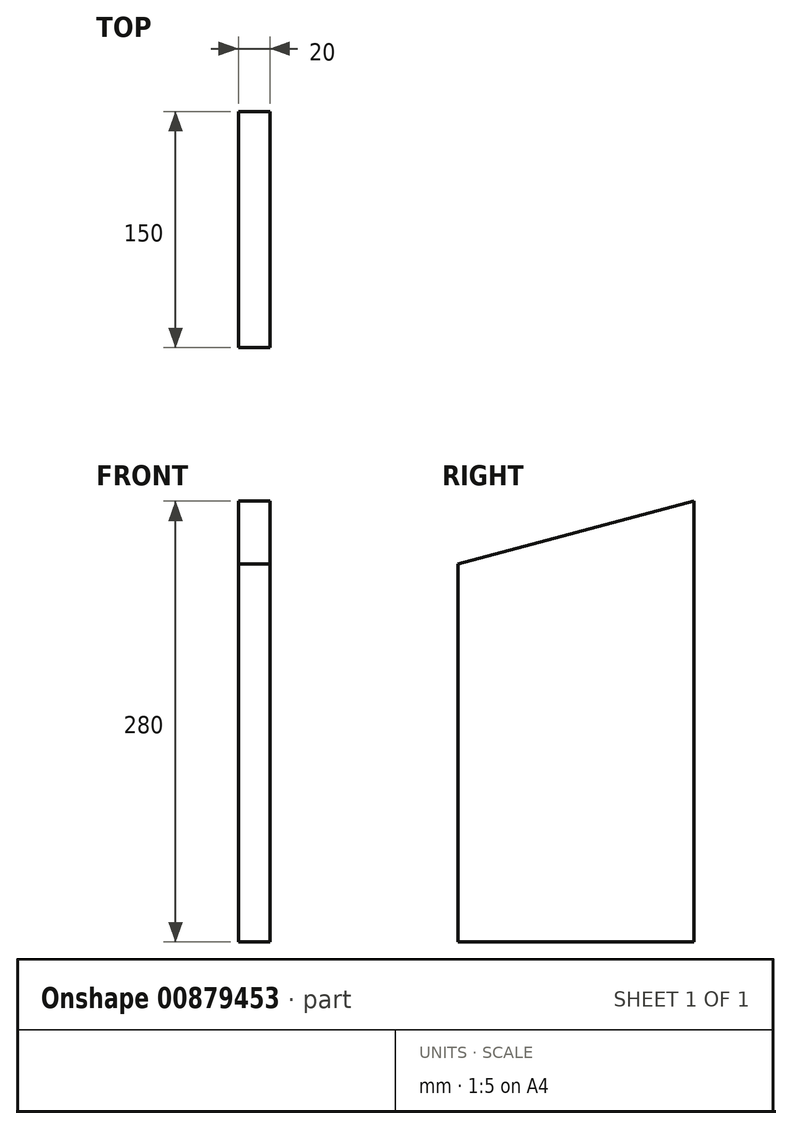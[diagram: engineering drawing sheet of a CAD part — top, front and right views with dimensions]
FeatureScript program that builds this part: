
annotation { "Feature Type Name" : "Feature", "Feature Type Description" : "" }
export const myFeature = defineFeature(function(context is Context, id is Id, definition is map)
    precondition{}
    {
        {
            var Q0;
            Q0=qCreatedBy(makeId("Right.planeOp"),FACE);
            var sketch = newSketch(context, id + "F0", { "sketchPlane" : qUnion([Q0])});
            skLineSegment(sketch, "E0.top", {"start": v(75, -140) * mm, "end": v(-75, -140) * mm});
            skLineSegment(sketch, "E0.left", {"start": v(75, 140) * mm, "end": v(75, -140) * mm});
            skLineSegment(sketch, "E0.right", {"start": v(-75, 100) * mm, "end": v(-75, -140) * mm});
            skPoint(sketch, "E0.middle", {"position": v(0, 0) * mm});
            skLineSegment(sketch, "E1", {"start": v(-75, 100) * mm, "end": v(75, 140) * mm});
            skSolve(sketch);
        }
        {
            var Q0;
            Q0=makeQuery(id+"F0.imprint","IMPRINT",FACE,{"disambiguationData":[TD([[makeQuery(id+"F0.imprint","IMPRINT",EDGE,{"derivedFrom":sQuery(id+"F0.wireOp",EDGE,"E0.top")}),-1.0]])]});
            extrude(context, id + "F1", {"entities" : qUnion([Q0]), "endBound" : BoundingType.SYMMETRIC, "depth" : 20 * mm, "offsetDistance" : 25 * mm});
        }
        {
            var Q0;
            Q0=makeQuery(id+"F1.opExtrude","CAP_FACE",FACE,{"disambiguationData":[OSD([sQuery(id+"F0.wireOp",EDGE,"E0.top"),sQuery(id+"F0.wireOp",EDGE,"E0.left"),sQuery(id+"F0.wireOp",EDGE,"E0.right"),sQuery(id+"F0.wireOp",EDGE,"E1")])],"isStart":false});
            var sketch = newSketch(context, id + "F2", { "sketchPlane" : qUnion([Q0])});
            skCircle(sketch, "E2", {"center": v(-65, -120) * mm, "radius": 5 * mm});
            skCircle(sketch, "E3", {"center": v(-65, 90) * mm, "radius": 5 * mm});
            skSolve(sketch);
        }
        {
            var Q0;
            Q0=makeQuery(id+"F1.opExtrude","CAP_FACE",FACE,{"disambiguationData":[OSD([sQuery(id+"F0.wireOp",EDGE,"E0.top"),sQuery(id+"F0.wireOp",EDGE,"E0.left"),sQuery(id+"F0.wireOp",EDGE,"E0.right"),sQuery(id+"F0.wireOp",EDGE,"E1")])],"isStart":true});
            var sketch = newSketch(context, id + "F3", { "sketchPlane" : qUnion([Q0])});
            skCircle(sketch, "E4", {"center": v(65, -120) * mm, "radius": 5 * mm});
            skCircle(sketch, "E5", {"center": v(65, 90) * mm, "radius": 5 * mm});
            skSolve(sketch);
        }
        {
            var Q0;
            Q0=makeQuery(id+"F1.opExtrude","SWEPT_FACE",FACE,{"disambiguationData":[OSD([sQuery(id+"F0.wireOp",EDGE,"E0.left")])]});
            var sketch = newSketch(context, id + "F4", { "sketchPlane" : qUnion([Q0])});
            skCircle(sketch, "E6", {"center": v(0, -120) * mm, "radius": 5 * mm});
            skPoint(sketch, "E6.centerSnap0", {"position": v(0, -140) * mm});
            skCircle(sketch, "E7", {"center": v(0, 120) * mm, "radius": 5 * mm});
            skPoint(sketch, "E7.centerSnap0", {"position": v(0, 140) * mm});
            skSolve(sketch);
        }
        {
            var Q0;
            Q0=makeQuery(id+"F1.opExtrude","CAP_FACE",FACE,{"disambiguationData":[OSD([sQuery(id+"F0.wireOp",EDGE,"E0.top"),sQuery(id+"F0.wireOp",EDGE,"E0.left"),sQuery(id+"F0.wireOp",EDGE,"E0.right"),sQuery(id+"F0.wireOp",EDGE,"E1")])],"isStart":false});
            var sketch = newSketch(context, id + "F5", { "sketchPlane" : qUnion([Q0])});
            skCircle(sketch, "E8", {"center": v(-35, -130) * mm, "radius": 5 * mm});
            skSolve(sketch);
        }
    });
